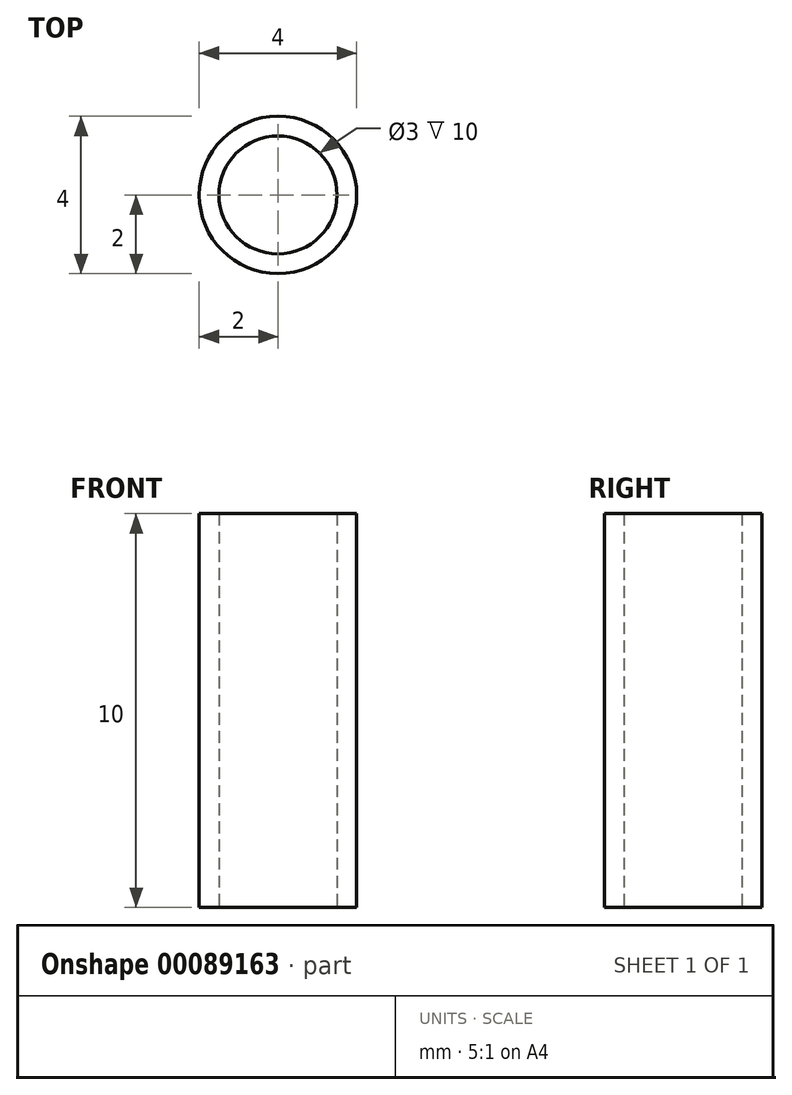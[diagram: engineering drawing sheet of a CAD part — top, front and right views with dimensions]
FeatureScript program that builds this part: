
annotation { "Feature Type Name" : "Feature", "Feature Type Description" : "" }
export const myFeature = defineFeature(function(context is Context, id is Id, definition is map)
    precondition{}
    {
        {
            var Q0;
            Q0=qCreatedBy(makeId("Top.planeOp"),FACE);
            var sketch = newSketch(context, id + "F0", { "sketchPlane" : qUnion([Q0])});
            skCircle(sketch, "E0", {"center": v(0, 0) * mm, "radius": 2 * mm});
            skCircle(sketch, "E1", {"center": v(0, 0) * mm, "radius": 1.5 * mm});
            skSolve(sketch);
        }
        {
            var Q0;
            Q0 = qSketchRegion(id + "F0", true);
            extrude(context, id + "F1", {"entities" : qUnion([Q0]), "depth" : 10 * mm});
        }
    });
